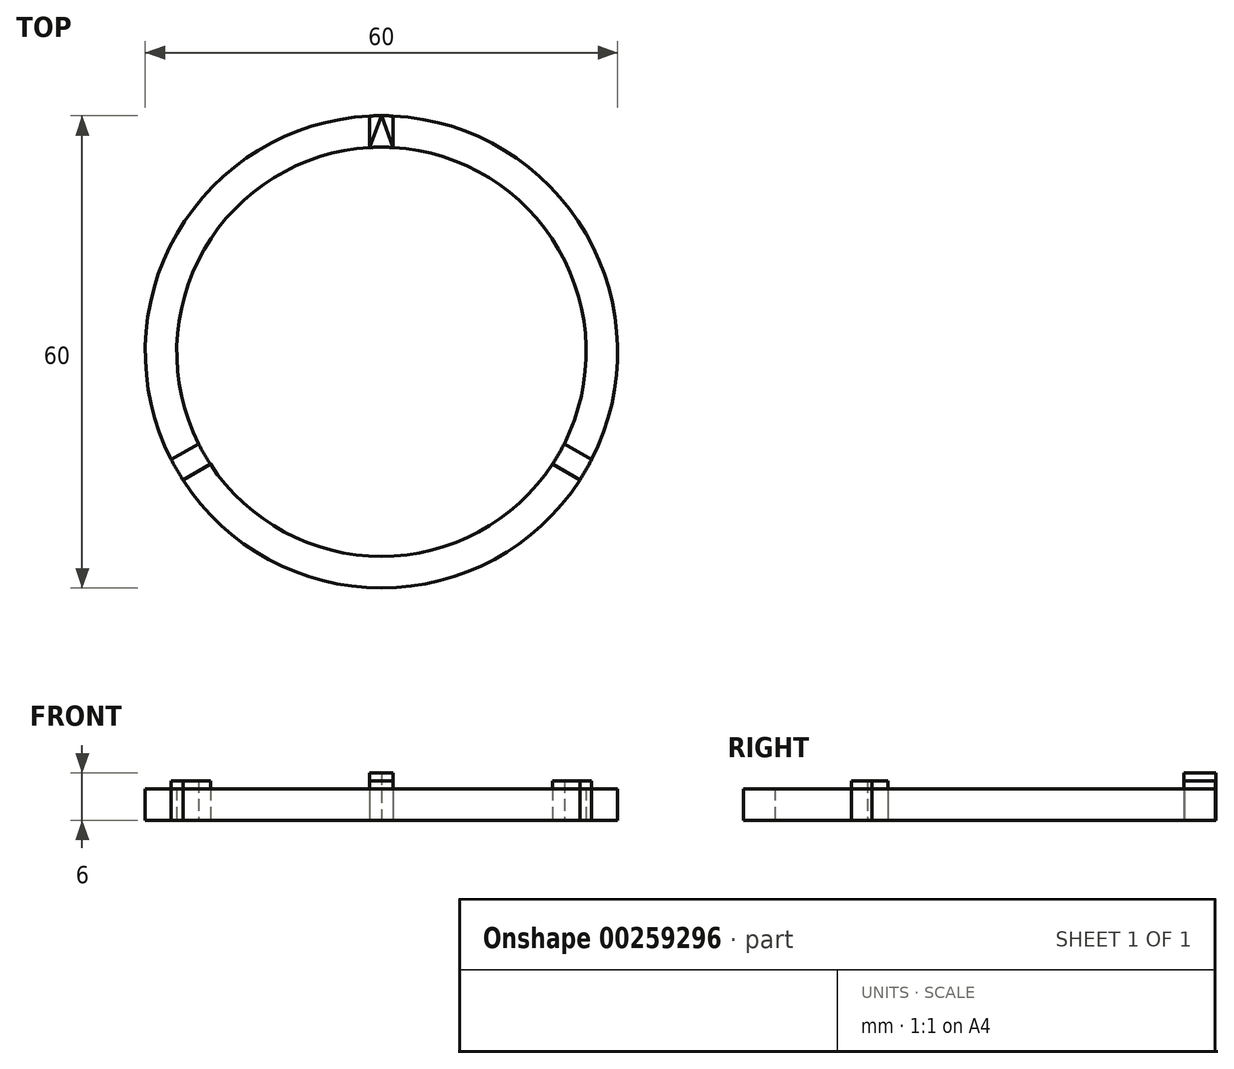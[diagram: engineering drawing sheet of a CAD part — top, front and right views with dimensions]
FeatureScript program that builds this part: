
annotation { "Feature Type Name" : "Feature", "Feature Type Description" : "" }
export const myFeature = defineFeature(function(context is Context, id is Id, definition is map)
    precondition{}
    {
        {
            var Q0;
            Q0=qCreatedBy(makeId("Top.planeOp"),FACE);
            var sketch = newSketch(context, id + "F0", { "sketchPlane" : qUnion([Q0])});
            skCircle(sketch, "E0", {"center": v(0, 0) * mm, "radius": 30 * mm});
            skCircle(sketch, "E1", {"center": v(0, 0) * mm, "radius": 26 * mm});
            skLineSegment(sketch, "E2", {"start": v(0, 26) * mm, "end": v(0, 30) * mm});
            skLineSegment(sketch, "E3.0", {"start": v(1.5, 25.96) * mm, "end": v(1.5, 29.96) * mm});
            skLineSegment(sketch, "E4.MirrorCS", {"start": v(-1.5, 25.96) * mm, "end": v(-1.5, 29.96) * mm});
            skLineSegment(sketch, "E5", {"start": v(-1.5, 25.96) * mm, "end": v(0, 30) * mm});
            skLineSegment(sketch, "E6", {"start": v(1.5, 25.96) * mm, "end": v(0, 30) * mm});
            skSolve(sketch);
        }
        {
            var Q0;
            Q0=makeQuery(id+"F0.imprint","IMPRINT",FACE,{"disambiguationData":[TD([[makeQuery(id+"F0.imprint","IMPRINT",EDGE,{"derivedFrom":sQuery(id+"F0.wireOp",EDGE,"E0")}),1.0]])]});
            var Q1;
            {var subQ0=sQuery(id+"F0.wireOp",EDGE,"E2");Q1=makeQuery(id+"F0.imprint","IMPRINT",FACE,{"disambiguationData":[TD([[makeQuery(id+"F0.imprint","IMPRINT",EDGE,{"derivedFrom":subQ0}),1.0]])]});}
            var Q2;
            {var subQ0=sQuery(id+"F0.wireOp",EDGE,"E2");Q2=makeQuery(id+"F0.imprint","IMPRINT",FACE,{"disambiguationData":[TD([[makeQuery(id+"F0.imprint","IMPRINT",EDGE,{"derivedFrom":subQ0}),-1.0]])]});}
            extrude(context, id + "F1", {"entities" : qUnion([Q0, Q1, Q2]), "depth" : 5 * mm});
        }
        {
            var Q0;
            Q0=makeQuery(id+"F0.imprint","IMPRINT",FACE,{"disambiguationData":[TD([[makeQuery(id+"F0.imprint","IMPRINT",EDGE,{"derivedFrom":sQuery(id+"F0.wireOp",EDGE,"b4Wjgr69-LSCB-HOO6-itIu-AQmrdIyT1RJC")}),1.0]])]});
            var Q1;
            {var subQ0=sQuery(id+"F0.wireOp",EDGE,"E2");Q1=makeQuery(id+"F0.imprint","IMPRINT",FACE,{"disambiguationData":[TD([[makeQuery(id+"F0.imprint","IMPRINT",EDGE,{"derivedFrom":subQ0}),-1.0]])]});}
            var Q2;
            {var subQ0=sQuery(id+"F0.wireOp",EDGE,"E2");Q2=makeQuery(id+"F0.imprint","IMPRINT",FACE,{"disambiguationData":[TD([[makeQuery(id+"F0.imprint","IMPRINT",EDGE,{"derivedFrom":subQ0}),1.0]])]});}
            extrude(context, id + "F2", {"entities" : qUnion([Q0, Q1, Q2]), "depth" : 6 * mm});
        }
        {
            var Q0;
            Q0=makeQuery(id+"F1.opExtrude","SWEPT_BODY",BODY,{"disambiguationData":[OSD([sQuery(id+"F0.wireOp",EDGE,"E0"),sQuery(id+"F0.wireOp",EDGE,"E1"),sQuery(id+"F0.wireOp",EDGE,"E3.0"),sQuery(id+"F0.wireOp",EDGE,"E4.MirrorCS")])]});
            var Q1;
            Q1=makeQuery(id+"F1.opExtrude","SWEPT_FACE",FACE,{"disambiguationData":[OSD([sQuery(id+"F0.wireOp",EDGE,"E1")])]});
            circularPattern(context, id + "F3", {"entities" : qUnion([Q0]), "axis" : qUnion([Q1]), "angle" : 360 * degree, "instanceCount" : 3, "equalSpace" : true});
        }
        {
            var Q0;
            {var subQ0=sQuery(id+"F0.wireOp",EDGE,"E3.0");Q0=makeQuery(id+"F0.imprint","IMPRINT",FACE,{"disambiguationData":[TD([[makeQuery(id+"F0.imprint","IMPRINT",EDGE,{"derivedFrom":subQ0}),-1.0]])]});}
            extrude(context, id + "F4", {"entities" : qUnion([Q0]), "depth" : 4 * mm});
        }
    });
